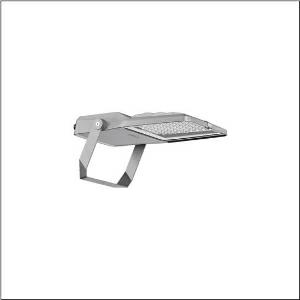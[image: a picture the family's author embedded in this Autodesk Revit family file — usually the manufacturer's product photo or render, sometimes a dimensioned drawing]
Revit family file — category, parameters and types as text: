
# Revit family: floodlight_fl_21_iq_mini___pl64_5xa7772c3e1a_c8ef
name_source: partatom
category: Lighting Fixtures
units: mm (PartAtom-declared; Revit-internal decimal feet)

## family parameters
Cut with Voids When Loaded = No
Host = Face
Light Source = No
Part Type = Normal
Room Calculation Point = No
Round Connector Dimension = Use Diameter
Shared = No

## types (1)
- --- (1 x LED, 10150 lm, 87.2 W, 3000K)
    Apparent Load = 87 VA
    CIE Flux Codes = 28 80 98 100 100
    Color Rendering = 80
    Color Temperature = 3000K
    Default Elevation = 1800 mm
    Description = Floodlight FL 21 iQ mini, floodlight, primary light control with lens, of PMMA, primary optical cover: protective disc, of toughened safety glass, transparent, light distribution: PL64, light emission: direct distribution, installation type: surface-mounted, LED, High Power LED, rated luminous flux: 10.150lm, luminous efficacy: 116lm/W, light colour: 830, colour temperature: 3000K, control gear: iQ Street-Remote/DALI, control: Street-Remote, Auto-Match, Temp-Guard, Night-Set, Smart-Wire, Desk-Remote (wireless, voltage-free reading and setting of iQ features in the workshop via application-optimized NFC function/RFID function), optimised constant luminous flux control (CLO 2.0), with terminal, 6-pole, mains connection: 220..240V, AC, 50/60Hz, start of lifetime: 87W, end of service life: 92W, reduction: 40W, luminaire housing, of diecast aluminium, powder-coated, Siteco® metallic grey (DB 702S), corrosivity category C5 mid according to DIN EN ISO 12944, suitable for swimming pools, chlorine-resistant, sealing non-destructively replaceable, mounting bracket, of steel, galvanised, powder-coated, Siteco® metallic grey (DB 702S), protection rating (complete): IP66, insulation class (complete): insulation class II (safety insulation), certification: CE, ENEC, VDE, protection symbol: D, impact resistance: IK08, permissible operating ambient temperature: -40..+40°C, permissible operating ambient temperature for outdoor applications: -40..+50°C, standard: DIN EN 12944, LABS conformity tested according to VDMA 24364:2018-05, packaging unit: 1 piece

Light Distribution: PL64
    Height = 70 mm
    Lamp = 1 x LED
    Lamp Light Flux = 10150 lm
    Lamp Power = 87.2 W
    Lamp count = 1
    Length = 485 mm
    Luminous efficacy = 116 lm/W
    Manufacturer = Siteco
    ModVariant = No
    Model = 5XA7772C3E1A
    Number of Poles = 1
    OnlyDefault = Yes
    Power Factor = 1
    Product Name = Floodlight FL 21 iQ mini | PL64
    Product group = floodlight | pylon annexe
    ProductGroupID = 6200
    Protection Class = Protection class II
    Protection Degree = IP 66
    RLX_Detail_Level = 1
    RLX_Emergency_Light_Flux = 0 lm
    RLX_Emergency_Type = 0
    RLX_Emergency_Type_DB = No
    RlxData = <blob elided: 96341 chars, md5=397bce4a>
    Socket = socket
    Standby Power = 0 W
    System Light Flux = 10150 lm
    System Power = 87 W
    Type Comments = factory setting: luminous flux: 100 % | dim-lin: 254 | 456 mA
    Type Image = l_1006845.jpg
    URL = http://relux.com
    VarID = @adj_166326
    Voltage = 0 V
    Weight = 0.00 kg
    Width = 337 mm

## geometry (parser evidence)
native form markers: Blend x4, Sweep x12
no freeform markers — native parametric forms only
